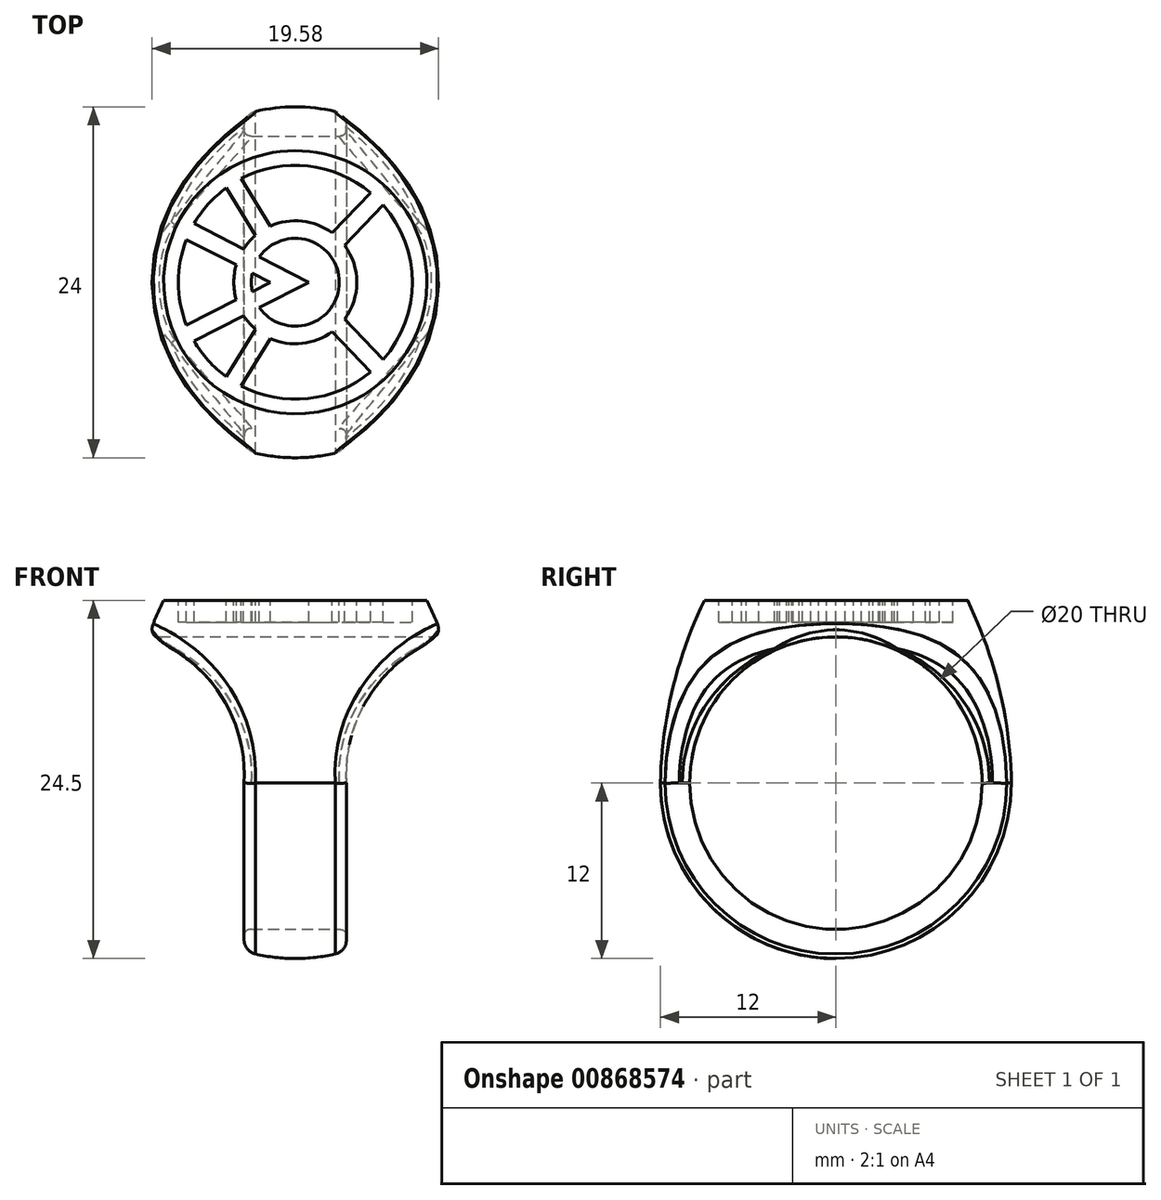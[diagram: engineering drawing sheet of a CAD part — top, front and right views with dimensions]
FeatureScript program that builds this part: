
annotation { "Feature Type Name" : "Feature", "Feature Type Description" : "" }
export const myFeature = defineFeature(function(context is Context, id is Id, definition is map)
    precondition{}
    {
        {
            var Q0;
            Q0=qCreatedBy(makeId("Right.planeOp"),FACE);
            var sketch = newSketch(context, id + "F0", { "sketchPlane" : qUnion([Q0])});
            skLineSegment(sketch, "E0", {"start": v(0, 0) * mm, "end": v(0, -24.5) * mm});
            skLineSegment(sketch, "E1", {"start": v(0, 0) * mm, "end": v(-9, 0) * mm});
            skArc(sketch, "E2", {"start": v(-12, -12.5) * mm, "mid": v(-8.49, -20.99) * mm, "end": v(0, -24.5) * mm});
            skLineSegment(sketch, "E3", {"start": v(0, -12.5) * mm, "end": v(-12, -12.5) * mm, "construction": true});
            skArc(sketch, "E4", {"start": v(-9, 0) * mm, "mid": v(-11.18, -6.09) * mm, "end": v(-12, -12.5) * mm});
            skSolve(sketch);
        }
        {
            var Q0;
            Q0=makeQuery(id+"F0.imprint","IMPRINT",FACE,{"disambiguationData":[TD([[makeQuery(id+"F0.imprint","IMPRINT",EDGE,{"derivedFrom":sQuery(id+"F0.wireOp",EDGE,"E0")}),-1.0]])]});
            var Q1;
            Q1=sQuery(id+"F0.wireOp",EDGE,"E0");
            revolve(context, id + "F1", {"entities" : qUnion([Q0]), "axis" : qUnion([Q1]), "revolveType" : RevolveType.FULL});
        }
        {
            var Q0;
            Q0=qCreatedBy(makeId("Right.planeOp"),FACE);
            var sketch = newSketch(context, id + "F2", { "sketchPlane" : qUnion([Q0])});
            skCircle(sketch, "E5", {"center": v(0, -12.5) * mm, "radius": 10 * mm});
            skSolve(sketch);
        }
        {
            var Q0;
            Q0=qSketchRegion(id+"F2",true);
            extrude(context, id + "F3", {"entities" : qUnion([Q0]), "operationType" : NewBodyOperationType.REMOVE, "endBound" : BoundingType.SYMMETRIC, "oppositeDirection" : true, "depth" : 25 * mm, "offsetDistance" : 25 * mm});
        }
        {
            var Q0;
            Q0=qCreatedBy(makeId("Front.planeOp"),FACE);
            var sketch = newSketch(context, id + "F4", { "sketchPlane" : qUnion([Q0])});
            skLineSegment(sketch, "E6", {"start": v(3.5, -26.5) * mm, "end": v(3.5, -12.5) * mm});
            skArc(sketch, "E7", {"start": v(10.15, -2.5) * mm, "mid": v(5.16, -6.39) * mm, "end": v(3.5, -12.5) * mm});
            skLineSegment(sketch, "E8", {"start": v(10.15, -2.5) * mm, "end": v(11.65, -2.5) * mm});
            skLineSegment(sketch, "E9", {"start": v(11.65, -2.5) * mm, "end": v(11.65, -26.5) * mm});
            skLineSegment(sketch, "E10", {"start": v(11.65, -26.5) * mm, "end": v(3.5, -26.5) * mm});
            skPoint(sketch, "E11.start.orphan", {"position": v(0, -24.5) * mm});
            skLineSegment(sketch, "E12", {"start": v(0, 0) * mm, "end": v(0, -24.5) * mm, "construction": true});
            skLineSegment(sketch, "E13.MirrorCS", {"start": v(-3.5, -26.5) * mm, "end": v(-3.5, -12.5) * mm});
            skArc(sketch, "E14.MirrorCS", {"start": v(-10.15, -2.5) * mm, "mid": v(-5.16, -6.39) * mm, "end": v(-3.5, -12.5) * mm});
            skLineSegment(sketch, "E15.MirrorCS", {"start": v(-11.65, -2.5) * mm, "end": v(-11.65, -26.5) * mm});
            skLineSegment(sketch, "E16.MirrorCS", {"start": v(-11.65, -26.5) * mm, "end": v(-3.5, -26.5) * mm});
            skLineSegment(sketch, "E17.MirrorCS", {"start": v(-10.15, -2.5) * mm, "end": v(-11.65, -2.5) * mm});
            skSolve(sketch);
        }
        {
            var Q0;
            Q0=qSketchRegion(id+"F4",true);
            extrude(context, id + "F5", {"entities" : qUnion([Q0]), "operationType" : NewBodyOperationType.REMOVE, "endBound" : BoundingType.SYMMETRIC, "depth" : 25 * mm, "offsetDistance" : 25 * mm});
        }
        {
            var Q0;
            Q0=makeQuery(id+"F1.opRevolve","SWEPT_FACE",FACE,{"disambiguationData":[OSD([sQuery(id+"F0.wireOp",EDGE,"E1")])]});
            var sketch = newSketch(context, id + "F6", { "sketchPlane" : qUnion([Q0])});
            skArc(sketch, "E18", {"start": v(-7.45, 2.93) * mm, "mid": v(-8, 0) * mm, "end": v(-7.45, -2.93) * mm});
            skLineSegment(sketch, "E19", {"start": v(-8, 0) * mm, "end": v(8, 0) * mm, "construction": true});
            skArc(sketch, "E20", {"start": v(3, 0) * mm, "mid": v(0.9, 2.87) * mm, "end": v(-2.46, 1.73) * mm});
            skArc(sketch, "E21", {"start": v(4.2, 0) * mm, "mid": v(4, 1.33) * mm, "end": v(3.36, 2.53) * mm});
            skLineSegment(sketch, "E22", {"start": v(0.94, 0) * mm, "end": v(-2.46, 1.73) * mm});
            skLineSegment(sketch, "E23", {"start": v(-7.45, 2.93) * mm, "end": v(-4.04, 1.19) * mm});
            skLineSegment(sketch, "E24", {"start": v(-4.72, 6.46) * mm, "end": v(-2.72, 3.2) * mm});
            skLineSegment(sketch, "E25", {"start": v(-3.7, 7.09) * mm, "end": v(-1.7, 3.85) * mm});
            skLineSegment(sketch, "E26", {"start": v(5.15, 6.12) * mm, "end": v(2.51, 3.37) * mm});
            skLineSegment(sketch, "E27", {"start": v(6, 5.28) * mm, "end": v(3.36, 2.53) * mm});
            skArc(sketch, "E28.trimOffspring", {"start": v(-4.04, 1.19) * mm, "mid": v(-4.16, 0.6) * mm, "end": v(-4.2, 0) * mm});
            skArc(sketch, "E29.trimOffspring", {"start": v(-2.94, 0.63) * mm, "mid": v(-2.99, 0.32) * mm, "end": v(-3, 0) * mm});
            skLineSegment(sketch, "E30.trimOffspring", {"start": v(-3.53, 2.28) * mm, "end": v(-6.92, 4) * mm});
            skLineSegment(sketch, "E31.trimOffspring", {"start": v(-2.94, 0.63) * mm, "end": v(-1.7, 0) * mm});
            skArc(sketch, "E32.trimOffspring", {"start": v(-2.72, 3.2) * mm, "mid": v(-3.16, 2.77) * mm, "end": v(-3.53, 2.28) * mm});
            skArc(sketch, "E33.trimOffspring", {"start": v(-4.72, 6.46) * mm, "mid": v(-5.95, 5.35) * mm, "end": v(-6.92, 4) * mm});
            skArc(sketch, "E34.trimOffspring", {"start": v(5.15, 6.12) * mm, "mid": v(0.87, 7.95) * mm, "end": v(-3.7, 7.09) * mm});
            skArc(sketch, "E35.trimOffspring", {"start": v(2.51, 3.37) * mm, "mid": v(0.47, 4.18) * mm, "end": v(-1.7, 3.85) * mm});
            skLineSegment(sketch, "E36.MirrorCS", {"start": v(-7.45, -2.93) * mm, "end": v(-4.04, -1.19) * mm});
            skLineSegment(sketch, "E37.MirrorCS", {"start": v(-3.53, -2.28) * mm, "end": v(-6.92, -4) * mm});
            skArc(sketch, "E38.MirrorCS", {"start": v(-4.04, -1.19) * mm, "mid": v(-4.16, -0.6) * mm, "end": v(-4.2, 0) * mm});
            skLineSegment(sketch, "E39.MirrorCS", {"start": v(-2.94, -0.63) * mm, "end": v(-1.7, 0) * mm});
            skArc(sketch, "E40.MirrorCS", {"start": v(-2.94, -0.63) * mm, "mid": v(-2.99, -0.32) * mm, "end": v(-3, 0) * mm});
            skLineSegment(sketch, "E41.MirrorCS", {"start": v(0.94, 0) * mm, "end": v(-2.46, -1.73) * mm});
            skArc(sketch, "E42.MirrorCS", {"start": v(3, 0) * mm, "mid": v(0.9, -2.87) * mm, "end": v(-2.46, -1.73) * mm});
            skArc(sketch, "E43.MirrorCS", {"start": v(-2.72, -3.2) * mm, "mid": v(-3.16, -2.77) * mm, "end": v(-3.53, -2.28) * mm});
            skLineSegment(sketch, "E44.MirrorCS", {"start": v(-4.72, -6.46) * mm, "end": v(-2.72, -3.2) * mm});
            skLineSegment(sketch, "E45.MirrorCS", {"start": v(-3.7, -7.09) * mm, "end": v(-1.7, -3.85) * mm});
            skArc(sketch, "E46.MirrorCS", {"start": v(2.51, -3.37) * mm, "mid": v(0.47, -4.18) * mm, "end": v(-1.7, -3.85) * mm});
            skLineSegment(sketch, "E47.MirrorCS", {"start": v(5.15, -6.12) * mm, "end": v(2.51, -3.37) * mm});
            skLineSegment(sketch, "E48.MirrorCS", {"start": v(6, -5.28) * mm, "end": v(3.36, -2.53) * mm});
            skArc(sketch, "E49.MirrorCS", {"start": v(4.2, 0) * mm, "mid": v(4, -1.33) * mm, "end": v(3.36, -2.53) * mm});
            skArc(sketch, "E50.trimOffspring", {"start": v(-6.92, -4) * mm, "mid": v(-5.95, -5.35) * mm, "end": v(-4.72, -6.46) * mm});
            skArc(sketch, "E51.trimOffspring", {"start": v(-3.7, -7.09) * mm, "mid": v(0.87, -7.95) * mm, "end": v(5.15, -6.12) * mm});
            skArc(sketch, "E52.trimOffspring", {"start": v(6, -5.28) * mm, "mid": v(8, 0) * mm, "end": v(6, 5.28) * mm});
            skSolve(sketch);
        }
        {
            var Q0;
            Q0=qSketchRegion(id+"F6",true);
            var Q1;
            Q1=makeQuery(id+"F6.imprint","IMPRINT",FACE,{"disambiguationData":[TD([[makeQuery(id+"F6.imprint","IMPRINT",EDGE,{"derivedFrom":sQuery(id+"F6.wireOp",EDGE,"g20j87Mm-wGr7-AMiz-bI8b-qS7GuHKO57cL")}),1.0]])]});
            extrude(context, id + "F7", {"entities" : qUnion([Q0, Q1]), "operationType" : NewBodyOperationType.REMOVE, "oppositeDirection" : true, "depth" : 1.5 * mm, "offsetDistance" : 25 * mm});
        }
        {
            var Q0;
            Q0=makeQuery(id+"F5.boolean.opBoolean","INTERSECT",EDGE,{"disambiguationData":[OD(1.0)],"derivedFrom":[makeQuery(id+"F1.opRevolve","SWEPT_FACE",FACE,{"disambiguationData":[OSD([sQuery(id+"F0.wireOp",EDGE,"E4")])]}),makeQuery(id+"F5.opExtrude","SWEPT_FACE",FACE,{"disambiguationData":[OSD([sQuery(id+"F4.wireOp",EDGE,"E14.MirrorCS")])]})]});
            var Q1;
            Q1=makeQuery(id+"F5.boolean.opBoolean","INTERSECT",EDGE,{"derivedFrom":[makeQuery(id+"F1.opRevolve","SWEPT_FACE",FACE,{"disambiguationData":[OSD([sQuery(id+"F0.wireOp",EDGE,"E2")])]}),makeQuery(id+"F5.opExtrude","SWEPT_FACE",FACE,{"disambiguationData":[OSD([sQuery(id+"F4.wireOp",EDGE,"E13.MirrorCS")])]})]});
            var Q2;
            Q2=makeQuery(id+"F5.boolean.opBoolean","INTERSECT",EDGE,{"disambiguationData":[OD(1.0)],"derivedFrom":[makeQuery(id+"F1.opRevolve","SWEPT_FACE",FACE,{"disambiguationData":[OSD([sQuery(id+"F0.wireOp",EDGE,"E4")])]}),makeQuery(id+"F5.opExtrude","SWEPT_FACE",FACE,{"disambiguationData":[OSD([sQuery(id+"F4.wireOp",EDGE,"E7")])]})]});
            var Q3;
            Q3=makeQuery(id+"F5.boolean.opBoolean","INTERSECT",EDGE,{"derivedFrom":[makeQuery(id+"F1.opRevolve","SWEPT_FACE",FACE,{"disambiguationData":[OSD([sQuery(id+"F0.wireOp",EDGE,"E2")])]}),makeQuery(id+"F5.opExtrude","SWEPT_FACE",FACE,{"disambiguationData":[OSD([sQuery(id+"F4.wireOp",EDGE,"E6")])]})]});
            fillet(context, id + "F8", {"entities" : qUnion([Q0, Q1, Q2, Q3]), "radius" : 1 * mm, "allowEdgeOverflow" : false});
        }
        {
            var Q0;
            Q0=makeQuery(id+"F5.boolean.opBoolean","INTERSECT",EDGE,{"disambiguationData":[OD(1.0)],"derivedFrom":[makeQuery(id+"F3.boolean.opBoolean","COPY",FACE,{"derivedFrom":makeQuery(id+"F3.opExtrude","SWEPT_FACE",FACE,{"disambiguationData":[OSD([sQuery(id+"F2.wireOp",EDGE,"E5")])]})}),makeQuery(id+"F5.opExtrude","SWEPT_FACE",FACE,{"disambiguationData":[OSD([sQuery(id+"F4.wireOp",EDGE,"E14.MirrorCS")])]})]});
            var Q1;
            Q1=makeQuery(id+"F5.boolean.opBoolean","INTERSECT",EDGE,{"derivedFrom":[makeQuery(id+"F3.boolean.opBoolean","COPY",FACE,{"derivedFrom":makeQuery(id+"F3.opExtrude","SWEPT_FACE",FACE,{"disambiguationData":[OSD([sQuery(id+"F2.wireOp",EDGE,"E5")])]})}),makeQuery(id+"F5.opExtrude","SWEPT_FACE",FACE,{"disambiguationData":[OSD([sQuery(id+"F4.wireOp",EDGE,"E13.MirrorCS")])]})]});
            var Q2;
            Q2=makeQuery(id+"F5.boolean.opBoolean","INTERSECT",EDGE,{"disambiguationData":[OD(0.0)],"derivedFrom":[makeQuery(id+"F3.boolean.opBoolean","COPY",FACE,{"derivedFrom":makeQuery(id+"F3.opExtrude","SWEPT_FACE",FACE,{"disambiguationData":[OSD([sQuery(id+"F2.wireOp",EDGE,"E5")])]})}),makeQuery(id+"F5.opExtrude","SWEPT_FACE",FACE,{"disambiguationData":[OSD([sQuery(id+"F4.wireOp",EDGE,"E14.MirrorCS")])]})]});
            var Q3;
            Q3=makeQuery(id+"F5.boolean.opBoolean","INTERSECT",EDGE,{"disambiguationData":[OD(0.0)],"derivedFrom":[makeQuery(id+"F3.boolean.opBoolean","COPY",FACE,{"derivedFrom":makeQuery(id+"F3.opExtrude","SWEPT_FACE",FACE,{"disambiguationData":[OSD([sQuery(id+"F2.wireOp",EDGE,"E5")])]})}),makeQuery(id+"F5.opExtrude","SWEPT_FACE",FACE,{"disambiguationData":[OSD([sQuery(id+"F4.wireOp",EDGE,"E7")])]})]});
            var Q4;
            Q4=makeQuery(id+"F3.boolean.opBoolean","COPY",FACE,{"derivedFrom":makeQuery(id+"F3.opExtrude","SWEPT_FACE",FACE,{"disambiguationData":[OSD([sQuery(id+"F2.wireOp",EDGE,"E5")])]})});
            fillet(context, id + "F9", {"entities" : qUnion([Q0, Q1, Q2, Q3, Q4]), "radius" : .5 * mm, "rho" : 0.5, "crossSection" : FilletCrossSection.CONIC, "allowEdgeOverflow" : false});
        }
    });
